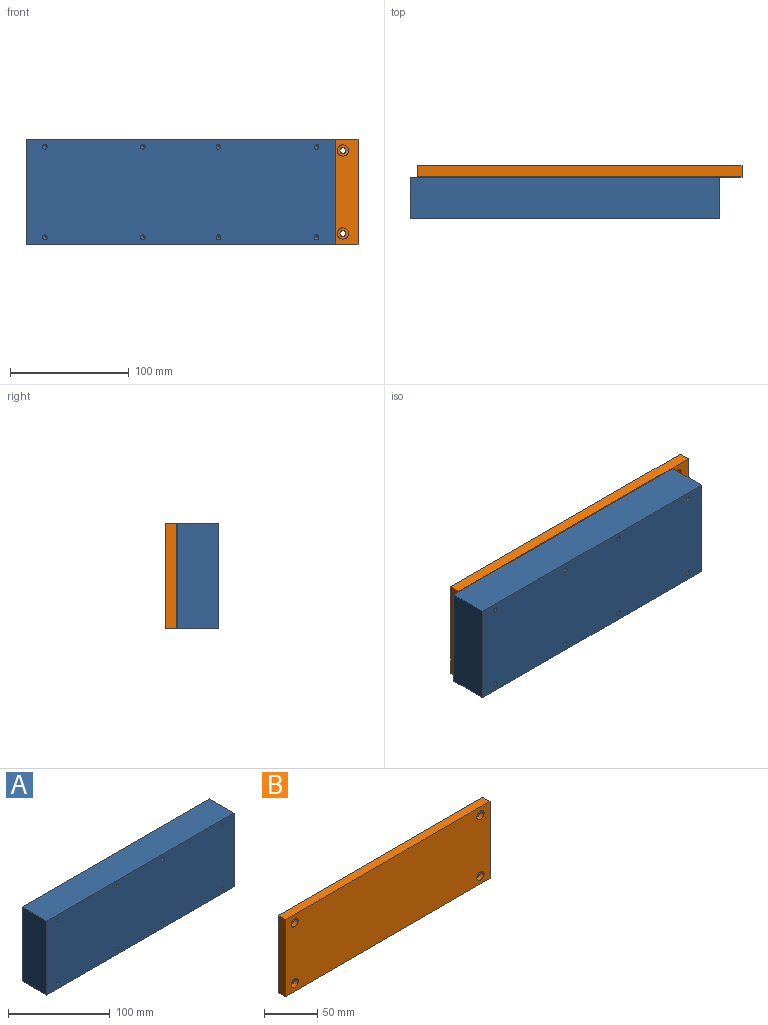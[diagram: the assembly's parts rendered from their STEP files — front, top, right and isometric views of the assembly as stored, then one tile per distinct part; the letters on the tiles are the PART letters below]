
ASSEMBLY  parts=2 mates=1
PART A: 22 faces, bbox 260.4x34.3x88.9 mm
  f0: plane 88.9x34.29mm, normal (1,0,0), area 3048.4mm2, adj f1,f3,f4,f5
  f1: plane 260.35x34.29mm, normal (0,0,1), area 8927.4mm2, adj f0,f2,f4,f5
  f2: plane 88.9x34.29mm, normal (-1,0,0), area 3048.4mm2, adj f1,f3,f4,f5
  f3: plane 260.35x34.29mm, normal (0,0,-1), area 8927.4mm2, adj f0,f2,f4,f5
  f4: plane 260.35x88.9mm, normal (0,1,0), area 23145.1mm2, adj f0,f1,f2,f3
  f5: plane 260.35x88.9mm, normal (0,-1,0), area 23042.6mm2, adj f0,f1,f2,f3,f6,f8,f10,f12
  f6: cylinder r=2.02mm len=21.43mm, axis (0,-1,0), area 271.9mm2, adj f5,f7
  f7: cone r=0mm half-angle=59deg, axis (0,-1,0), area 14.9mm2, adj f6
  f8: cylinder r=2.02mm len=21.43mm, axis (0,-1,0), area 271.9mm2, adj f5,f9
  f9: cone r=0mm half-angle=59deg, axis (0,-1,0), area 14.9mm2, adj f8
  f10: cylinder r=2.02mm len=21.43mm, axis (0,-1,0), area 271.9mm2, adj f5,f11
  f11: cone r=0mm half-angle=59deg, axis (0,-1,0), area 14.9mm2, adj f10
  f12: cylinder r=2.02mm len=21.43mm, axis (0,-1,0), area 271.9mm2, adj f5,f13
  f13: cone r=0mm half-angle=59deg, axis (0,-1,0), area 14.9mm2, adj f12
  f14: cylinder r=2.02mm len=21.43mm, axis (0,-1,0), area 271.9mm2, adj f5,f15
  f15: cone r=0mm half-angle=59deg, axis (0,-1,0), area 14.9mm2, adj f14
  f16: cylinder r=2.02mm len=21.43mm, axis (0,-1,0), area 271.9mm2, adj f5,f17
  f17: cone r=0mm half-angle=59deg, axis (0,-1,0), area 14.9mm2, adj f16
  f18: cylinder r=2.02mm len=21.43mm, axis (0,-1,0), area 271.9mm2, adj f5,f19
  f19: cone r=0mm half-angle=59deg, axis (0,-1,0), area 14.9mm2, adj f18
  f20: cylinder r=2.02mm len=21.43mm, axis (0,-1,0), area 271.9mm2, adj f5,f21
  f21: cone r=0mm half-angle=59deg, axis (0,-1,0), area 14.9mm2, adj f20
PART B: 18 faces, bbox 273.1x9.5x88.9 mm
  f0: plane 273.05x9.53mm, normal (0,0,-1), area 2600.8mm2, adj f1,f3,f4,f5
  f1: plane 88.9x9.53mm, normal (1,0,0), area 846.8mm2, adj f0,f2,f4,f5
  f2: plane 273.05x9.53mm, normal (0,0,1), area 2600.8mm2, adj f1,f3,f4,f5
  f3: plane 88.9x9.53mm, normal (-1,0,0), area 846.8mm2, adj f0,f2,f4,f5
  f4: plane 273.05x88.9mm, normal (0,1,0), area 24196.3mm2, adj f0,f1,f2,f3,f6,f9,f12,f15
  f5: plane 273.05x88.9mm, normal (0,-1,0), area 23989.1mm2, adj f0,f1,f2,f3,f8,f11,f14,f17
  f6: cylinder r=2.49mm len=4.98mm, axis (0,-1,0), area 73.5mm2, adj f4,f7
  f7: plane 9.53x9.53mm, normal (0,-1,0), area 51.8mm2, adj f6,f8
  f8: cylinder r=4.76mm len=9.53mm, axis (0,-1,0), area 144.4mm2, adj f5,f7
  f9: cylinder r=2.49mm len=4.98mm, axis (0,-1,0), area 73.5mm2, adj f4,f10
  f10: plane 9.53x9.53mm, normal (0,-1,0), area 51.8mm2, adj f9,f11
  f11: cylinder r=4.76mm len=9.53mm, axis (0,-1,0), area 144.4mm2, adj f5,f10
  f12: cylinder r=2.49mm len=4.98mm, axis (0,-1,0), area 73.5mm2, adj f4,f13
  f13: plane 9.53x9.53mm, normal (0,-1,0), area 51.8mm2, adj f12,f14
  f14: cylinder r=4.76mm len=9.53mm, axis (0,-1,0), area 144.4mm2, adj f5,f13
  f15: cylinder r=2.49mm len=4.98mm, axis (0,-1,0), area 73.5mm2, adj f4,f16
  f16: plane 9.53x9.53mm, normal (0,-1,0), area 51.8mm2, adj f15,f17
  f17: cylinder r=4.76mm len=9.53mm, axis (0,-1,0), area 144.4mm2, adj f5,f16
PLACE A t=(-12.69,-34.91,0.32)mm
PLACE B t=(0,0,0.32)mm fixed
MATE slider A.f0 <-> B.f1  axis (1,0,0) through (117.48,-17.77,0.32)mm
